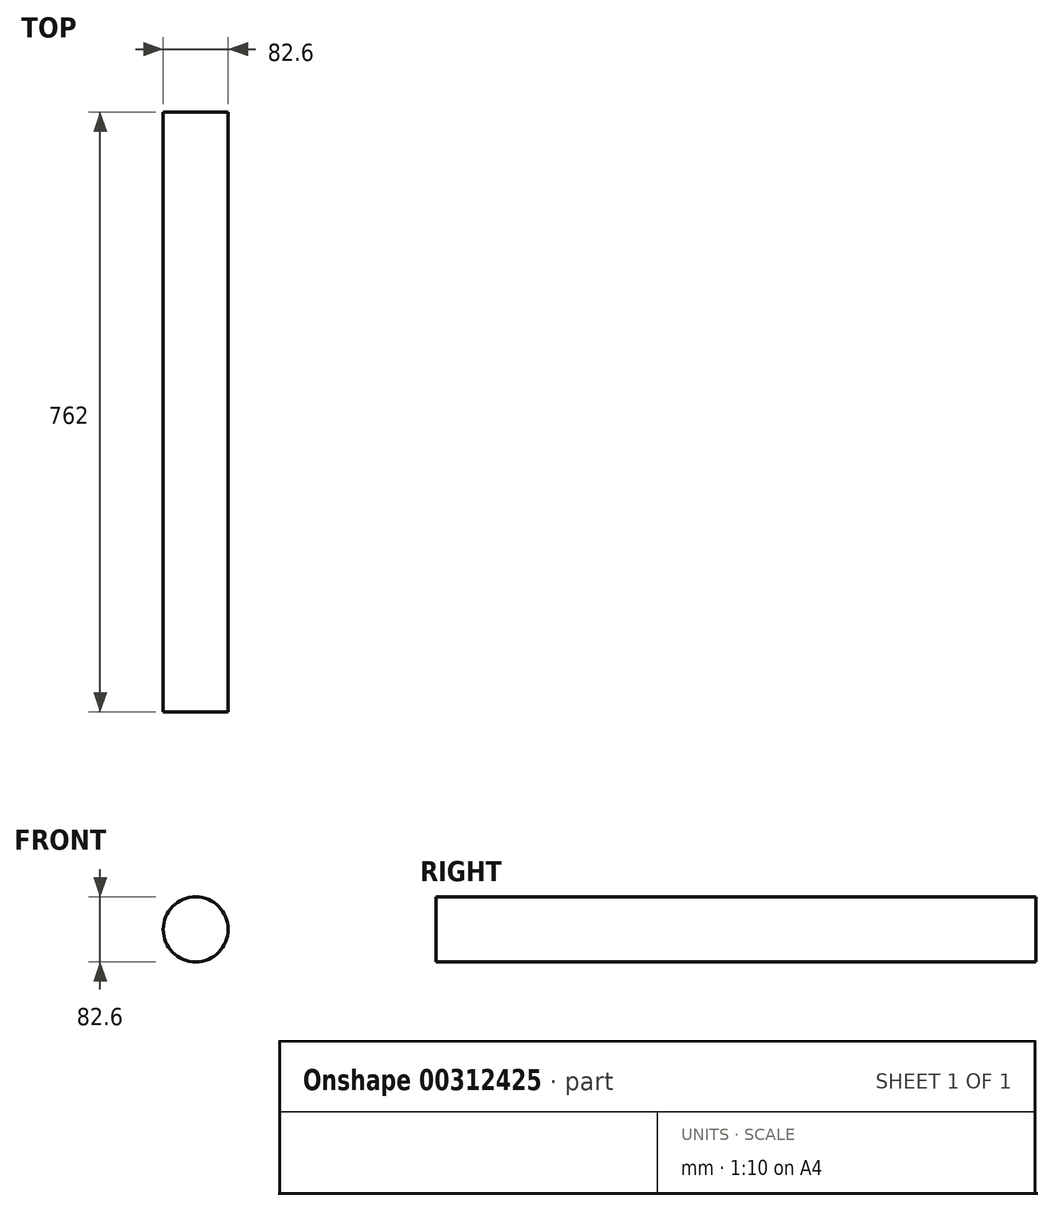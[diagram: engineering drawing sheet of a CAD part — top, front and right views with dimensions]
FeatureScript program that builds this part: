
annotation { "Feature Type Name" : "Feature", "Feature Type Description" : "" }
export const myFeature = defineFeature(function(context is Context, id is Id, definition is map)
    precondition{}
    {
        {
            var Q0;
            Q0=qCreatedBy(makeId("Front.planeOp"),FACE);
            var sketch = newSketch(context, id + "F0", { "sketchPlane" : qUnion([Q0])});
            skCircle(sketch, "E0", {"center": v(0, 0) * mm, "radius": 41.3 * mm});
            skSolve(sketch);
        }
        {
            var Q0;
            Q0=makeQuery(id+"F0.imprint","IMPRINT",FACE,{"disambiguationData":[TD([[makeQuery(id+"F0.imprint","IMPRINT",EDGE,{"derivedFrom":sQuery(id+"F0.wireOp",EDGE,"E0")}),1.0]])]});
            extrude(context, id + "F1", {"entities" : qUnion([Q0]), "depth" : 762 * mm});
        }
    });
